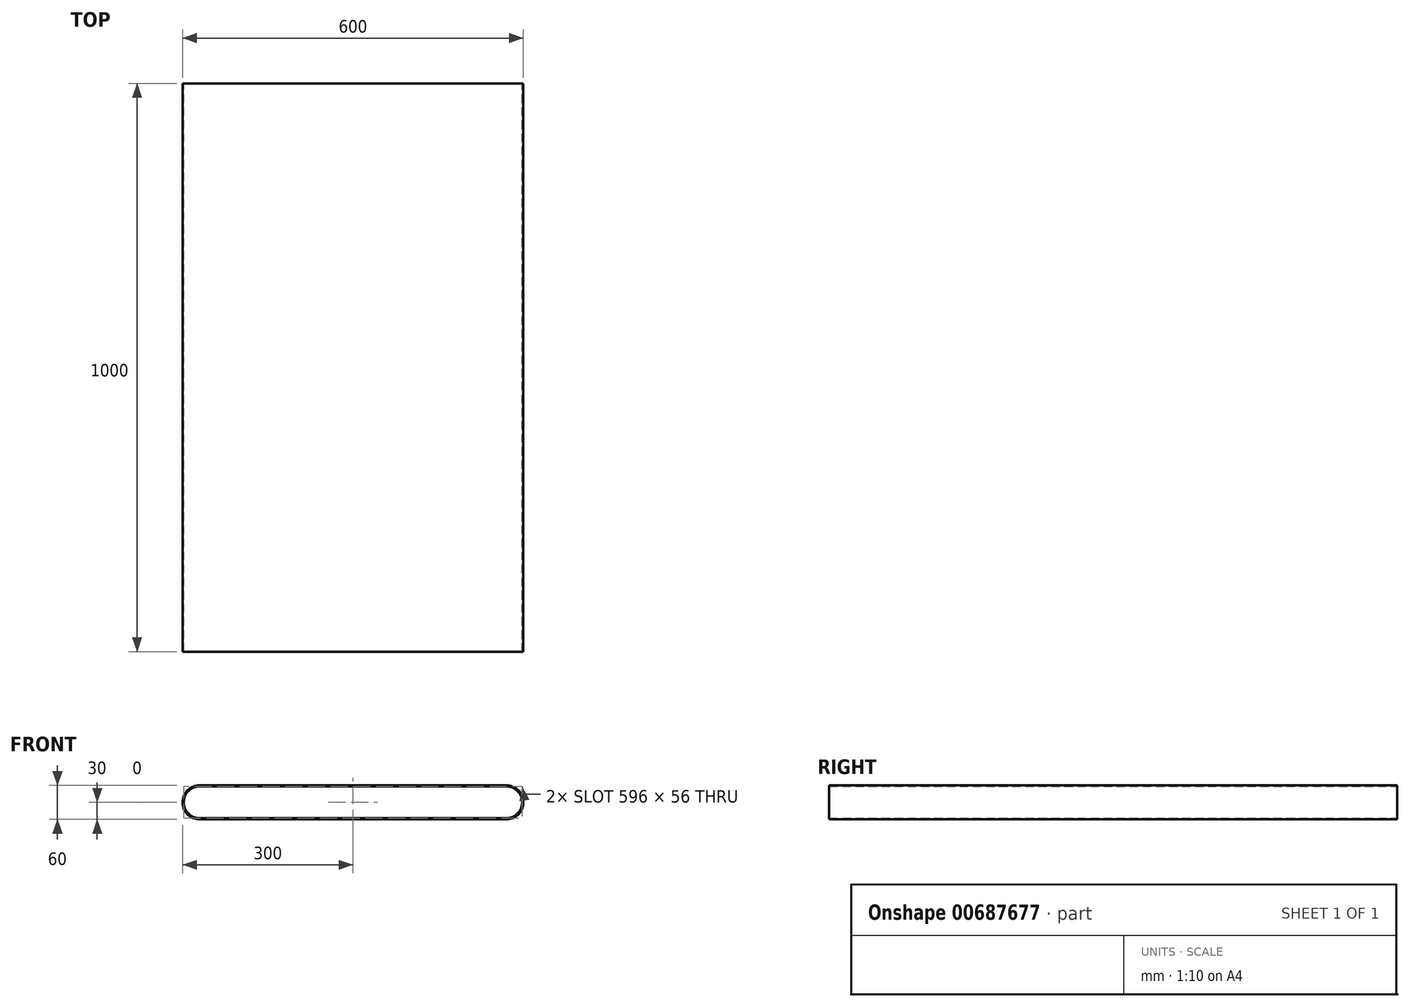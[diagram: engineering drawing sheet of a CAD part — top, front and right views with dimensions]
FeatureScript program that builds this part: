
annotation { "Feature Type Name" : "Feature", "Feature Type Description" : "" }
export const myFeature = defineFeature(function(context is Context, id is Id, definition is map)
    precondition{}
    {
        {
            var Q0;
            Q0=qCreatedBy(makeId("Front.planeOp"),FACE);
            var sketch = newSketch(context, id + "F0", { "sketchPlane" : qUnion([Q0])});
            skLineSegment(sketch, "E0", {"start": v(0, 0) * mm, "end": v(540, 0) * mm, "construction": true});
            skArc(sketch, "E1.0.startCap", {"start": v(0, -30) * mm, "mid": v(-30, 0) * mm, "end": v(0, 30) * mm});
            skArc(sketch, "E1.0.endCap", {"start": v(540, 30) * mm, "mid": v(570, 0) * mm, "end": v(540, -30) * mm});
            skLineSegment(sketch, "E1.0.left", {"start": v(0, 30) * mm, "end": v(540, 30) * mm});
            skLineSegment(sketch, "E1.0.right", {"start": v(0, -30) * mm, "end": v(540, -30) * mm});
            skArc(sketch, "E2.0.startCap", {"start": v(0, -28) * mm, "mid": v(-28, 0) * mm, "end": v(0, 28) * mm});
            skArc(sketch, "E2.0.endCap", {"start": v(540, 28) * mm, "mid": v(568, 0) * mm, "end": v(540, -28) * mm});
            skLineSegment(sketch, "E2.0.left", {"start": v(0, 28) * mm, "end": v(540, 28) * mm});
            skLineSegment(sketch, "E2.0.right", {"start": v(0, -28) * mm, "end": v(540, -28) * mm});
            skSolve(sketch);
        }
        {
            var Q0;
            Q0 = qSketchRegion(id + "F0", true);
            extrude(context, id + "F1", {"entities" : qUnion([Q0]), "depth" : 1000 * mm, "offsetDistance" : 25 * mm});
        }
    });
